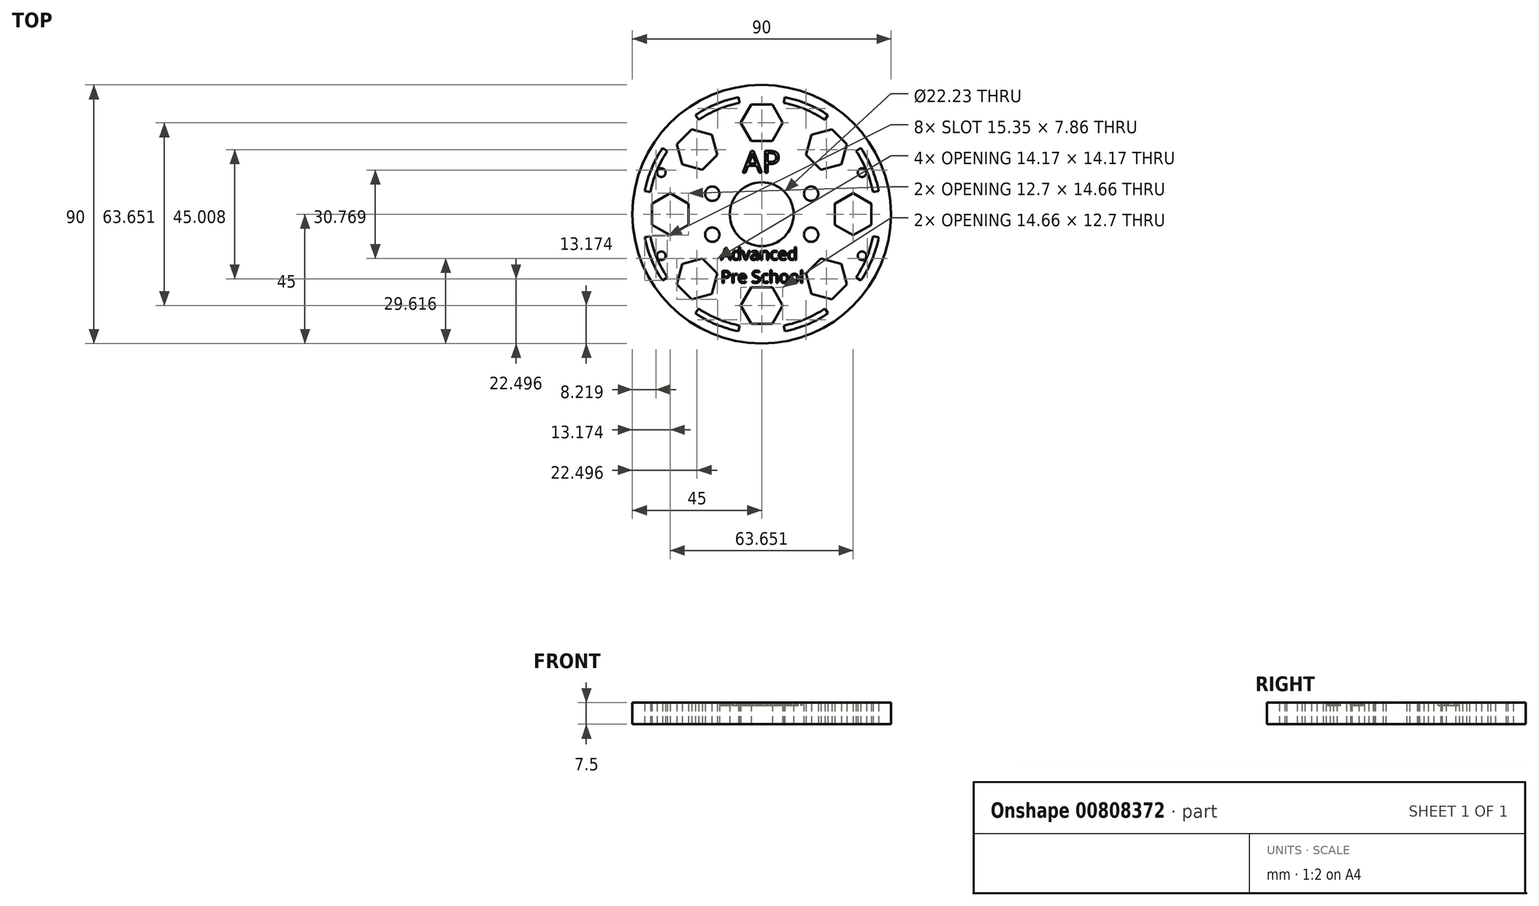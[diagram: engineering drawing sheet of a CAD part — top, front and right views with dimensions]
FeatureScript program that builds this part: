
annotation { "Feature Type Name" : "Feature", "Feature Type Description" : "" }
export const myFeature = defineFeature(function(context is Context, id is Id, definition is map)
    precondition{}
    {
        {
            var Q0;
            Q0=qCreatedBy(makeId("Top.planeOp"),FACE);
            var sketch = newSketch(context, id + "F0", { "sketchPlane" : qUnion([Q0])});
            skCircle(sketch, "E0", {"center": v(0, 0) * mm, "radius": 45 * mm});
            skCircle(sketch, "E1", {"center": v(0, 0) * mm, "radius": 11.11 * mm});
            skCircle(sketch, "E2", {"center": v(0, 31.83) * mm, "radius": 6.35 * mm});
            skCircle(sketch, "E3.cCircle", {"center": v(0, 31.83) * mm, "radius": 6.35 * mm, "construction": true});
            skLineSegment(sketch, "E3.0", {"start": v(-3.67, 38.18) * mm, "end": v(3.67, 38.18) * mm});
            skLineSegment(sketch, "E3.1", {"start": v(3.67, 38.18) * mm, "end": v(7.33, 31.83) * mm});
            skLineSegment(sketch, "E3.2", {"start": v(7.33, 31.83) * mm, "end": v(3.67, 25.48) * mm});
            skLineSegment(sketch, "E3.3", {"start": v(3.67, 25.48) * mm, "end": v(-3.67, 25.48) * mm});
            skLineSegment(sketch, "E3.4", {"start": v(-3.67, 25.48) * mm, "end": v(-7.33, 31.83) * mm});
            skLineSegment(sketch, "E3.5", {"start": v(-7.33, 31.83) * mm, "end": v(-3.67, 38.18) * mm});
            skPoint(sketch, "E3.0.midPoint", {"position": v(0, 38.18) * mm});
            skLineSegment(sketch, "E4.1.0", {"start": v(-15.42, 20.6) * mm, "end": v(-20.6, 15.42) * mm});
            skLineSegment(sketch, "E4.1.1", {"start": v(-17.32, 27.69) * mm, "end": v(-15.42, 20.6) * mm});
            skLineSegment(sketch, "E4.1.2", {"start": v(-20.6, 15.42) * mm, "end": v(-27.69, 17.32) * mm});
            skLineSegment(sketch, "E4.1.3", {"start": v(-27.69, 17.32) * mm, "end": v(-29.59, 24.4) * mm});
            skLineSegment(sketch, "E4.1.4", {"start": v(-29.59, 24.4) * mm, "end": v(-24.4, 29.59) * mm});
            skLineSegment(sketch, "E4.1.5", {"start": v(-24.4, 29.59) * mm, "end": v(-17.32, 27.69) * mm});
            skLineSegment(sketch, "E4.2.0", {"start": v(-25.48, 3.67) * mm, "end": v(-25.48, -3.67) * mm});
            skLineSegment(sketch, "E4.2.1", {"start": v(-31.83, 7.33) * mm, "end": v(-25.48, 3.67) * mm});
            skLineSegment(sketch, "E4.2.2", {"start": v(-25.48, -3.67) * mm, "end": v(-31.83, -7.33) * mm});
            skLineSegment(sketch, "E4.2.3", {"start": v(-31.83, -7.33) * mm, "end": v(-38.18, -3.67) * mm});
            skLineSegment(sketch, "E4.2.4", {"start": v(-38.18, -3.67) * mm, "end": v(-38.18, 3.67) * mm});
            skLineSegment(sketch, "E4.2.5", {"start": v(-38.18, 3.67) * mm, "end": v(-31.83, 7.33) * mm});
            skLineSegment(sketch, "E5.2.3.0", {"start": v(-20.6, -15.42) * mm, "end": v(-15.42, -20.6) * mm});
            skLineSegment(sketch, "E5.3.3.0", {"start": v(-27.69, -17.32) * mm, "end": v(-20.6, -15.42) * mm});
            skLineSegment(sketch, "E5.6.3.0", {"start": v(-15.42, -20.6) * mm, "end": v(-17.32, -27.69) * mm});
            skLineSegment(sketch, "E5.9.3.0", {"start": v(-17.32, -27.69) * mm, "end": v(-24.4, -29.59) * mm});
            skLineSegment(sketch, "E5.12.3.0", {"start": v(-24.4, -29.59) * mm, "end": v(-29.59, -24.4) * mm});
            skLineSegment(sketch, "E5.15.3.0", {"start": v(-29.59, -24.4) * mm, "end": v(-27.69, -17.32) * mm});
            skLineSegment(sketch, "E5.2.4.0", {"start": v(-3.67, -25.48) * mm, "end": v(3.67, -25.48) * mm});
            skLineSegment(sketch, "E5.3.4.0", {"start": v(-7.33, -31.83) * mm, "end": v(-3.67, -25.48) * mm});
            skLineSegment(sketch, "E5.6.4.0", {"start": v(3.67, -25.48) * mm, "end": v(7.33, -31.83) * mm});
            skLineSegment(sketch, "E5.9.4.0", {"start": v(7.33, -31.83) * mm, "end": v(3.67, -38.18) * mm});
            skLineSegment(sketch, "E5.12.4.0", {"start": v(3.67, -38.18) * mm, "end": v(-3.67, -38.18) * mm});
            skLineSegment(sketch, "E5.15.4.0", {"start": v(-3.67, -38.18) * mm, "end": v(-7.33, -31.83) * mm});
            skLineSegment(sketch, "E5.2.5.0", {"start": v(15.42, -20.6) * mm, "end": v(20.6, -15.42) * mm});
            skLineSegment(sketch, "E5.3.5.0", {"start": v(17.32, -27.69) * mm, "end": v(15.42, -20.6) * mm});
            skLineSegment(sketch, "E5.6.5.0", {"start": v(20.6, -15.42) * mm, "end": v(27.69, -17.32) * mm});
            skLineSegment(sketch, "E5.9.5.0", {"start": v(27.69, -17.32) * mm, "end": v(29.59, -24.4) * mm});
            skLineSegment(sketch, "E5.12.5.0", {"start": v(29.59, -24.4) * mm, "end": v(24.4, -29.59) * mm});
            skLineSegment(sketch, "E5.15.5.0", {"start": v(24.4, -29.59) * mm, "end": v(17.32, -27.69) * mm});
            skLineSegment(sketch, "E5.2.6.0", {"start": v(25.48, -3.67) * mm, "end": v(25.48, 3.67) * mm});
            skLineSegment(sketch, "E5.3.6.0", {"start": v(31.83, -7.33) * mm, "end": v(25.48, -3.67) * mm});
            skLineSegment(sketch, "E5.6.6.0", {"start": v(25.48, 3.67) * mm, "end": v(31.83, 7.33) * mm});
            skLineSegment(sketch, "E5.9.6.0", {"start": v(31.83, 7.33) * mm, "end": v(38.18, 3.67) * mm});
            skLineSegment(sketch, "E5.12.6.0", {"start": v(38.18, 3.67) * mm, "end": v(38.18, -3.67) * mm});
            skLineSegment(sketch, "E5.15.6.0", {"start": v(38.18, -3.67) * mm, "end": v(31.83, -7.33) * mm});
            skLineSegment(sketch, "E5.2.7.0", {"start": v(20.6, 15.42) * mm, "end": v(15.42, 20.6) * mm});
            skLineSegment(sketch, "E5.3.7.0", {"start": v(27.69, 17.32) * mm, "end": v(20.6, 15.42) * mm});
            skLineSegment(sketch, "E5.6.7.0", {"start": v(15.42, 20.6) * mm, "end": v(17.32, 27.69) * mm});
            skLineSegment(sketch, "E5.9.7.0", {"start": v(17.32, 27.69) * mm, "end": v(24.4, 29.59) * mm});
            skLineSegment(sketch, "E5.12.7.0", {"start": v(24.4, 29.59) * mm, "end": v(29.59, 24.4) * mm});
            skLineSegment(sketch, "E5.15.7.0", {"start": v(29.59, 24.4) * mm, "end": v(27.69, 17.32) * mm});
            skLineSegment(sketch, "E6.anchor2", {"start": v(0, 0) * mm, "end": v(41.57, -17.22) * mm, "construction": true});
            skCircle(sketch, "E7", {"center": v(17.2, -7.13) * mm, "radius": 2.5 * mm});
            skCircle(sketch, "E8", {"center": v(34.93, -14.47) * mm, "radius": 1.5 * mm});
            skCircle(sketch, "E9.MirrorC", {"center": v(34.93, 14.47) * mm, "radius": 1.5 * mm});
            skCircle(sketch, "E10.MirrorC", {"center": v(17.2, 7.13) * mm, "radius": 2.5 * mm});
            skCircle(sketch, "E11.MirrorC", {"center": v(-17.2, 7.13) * mm, "radius": 2.5 * mm});
            skCircle(sketch, "E12.MirrorC", {"center": v(-34.93, 14.47) * mm, "radius": 1.5 * mm});
            skCircle(sketch, "E13.MirrorC", {"center": v(-17.2, -7.13) * mm, "radius": 2.5 * mm});
            skCircle(sketch, "E14.MirrorC", {"center": v(-34.93, -14.47) * mm, "radius": 1.5 * mm});
            skLineSegment(sketch, "E15", {"start": v(0, 0) * mm, "end": v(0, -45) * mm});
            skLineSegment(sketch, "E16.1.0", {"start": v(0, 0) * mm, "end": v(-2.17, -10.9) * mm});
            skLineSegment(sketch, "E16.3.0", {"start": v(0, 0) * mm, "end": v(-18.76, -28.07) * mm});
            skArc(sketch, "E17", {"start": v(-7.7, -38.75) * mm, "mid": v(-15.12, -36.5) * mm, "end": v(-21.95, -32.85) * mm});
            skArc(sketch, "E18", {"start": v(-8.1, -40.71) * mm, "mid": v(-15.88, -38.35) * mm, "end": v(-23.06, -34.51) * mm});
            skLineSegment(sketch, "E19.trimOffspring", {"start": v(-5.8, -29.18) * mm, "end": v(-6.59, -33.12) * mm});
            skPoint(sketch, "E20.orphan", {"position": v(-25, -37.42) * mm});
            skLineSegment(sketch, "E21.trimOffspring", {"start": v(-21.95, -32.85) * mm, "end": v(-23.06, -34.51) * mm});
            skLineSegment(sketch, "E22.trimOffspring", {"start": v(-7.7, -38.75) * mm, "end": v(-8.1, -40.71) * mm});
            skPoint(sketch, "E23.orphan", {"position": v(-8.78, -44.14) * mm});
            skPoint(sketch, "E24.1.0", {"position": v(8.78, -44.14) * mm});
            skArc(sketch, "E24.1.1", {"start": v(21.95, -32.85) * mm, "mid": v(15.12, -36.5) * mm, "end": v(7.7, -38.75) * mm});
            skArc(sketch, "E24.1.2", {"start": v(23.06, -34.51) * mm, "mid": v(15.88, -38.35) * mm, "end": v(8.1, -40.71) * mm});
            skLineSegment(sketch, "E24.1.3", {"start": v(21.95, -32.85) * mm, "end": v(23.06, -34.51) * mm});
            skLineSegment(sketch, "E24.1.4", {"start": v(7.7, -38.75) * mm, "end": v(8.1, -40.71) * mm});
            skPoint(sketch, "E24.2.0", {"position": v(37.42, -25) * mm});
            skArc(sketch, "E24.2.1", {"start": v(38.75, -7.7) * mm, "mid": v(36.5, -15.12) * mm, "end": v(32.85, -21.95) * mm});
            skArc(sketch, "E24.2.2", {"start": v(40.71, -8.1) * mm, "mid": v(38.35, -15.88) * mm, "end": v(34.51, -23.06) * mm});
            skLineSegment(sketch, "E24.2.3", {"start": v(38.75, -7.7) * mm, "end": v(40.71, -8.1) * mm});
            skLineSegment(sketch, "E24.2.4", {"start": v(32.85, -21.95) * mm, "end": v(34.51, -23.06) * mm});
            skPoint(sketch, "E24.3.0", {"position": v(44.14, 8.78) * mm});
            skArc(sketch, "E24.3.1", {"start": v(32.85, 21.95) * mm, "mid": v(36.5, 15.12) * mm, "end": v(38.75, 7.7) * mm});
            skArc(sketch, "E24.3.2", {"start": v(34.51, 23.06) * mm, "mid": v(38.35, 15.88) * mm, "end": v(40.71, 8.1) * mm});
            skLineSegment(sketch, "E24.3.3", {"start": v(32.85, 21.95) * mm, "end": v(34.51, 23.06) * mm});
            skLineSegment(sketch, "E24.3.4", {"start": v(38.75, 7.7) * mm, "end": v(40.71, 8.1) * mm});
            skPoint(sketch, "E24.4.0", {"position": v(25, 37.42) * mm});
            skArc(sketch, "E24.4.1", {"start": v(7.7, 38.75) * mm, "mid": v(15.12, 36.5) * mm, "end": v(21.95, 32.85) * mm});
            skArc(sketch, "E24.4.2", {"start": v(8.1, 40.71) * mm, "mid": v(15.88, 38.35) * mm, "end": v(23.06, 34.51) * mm});
            skLineSegment(sketch, "E24.4.3", {"start": v(7.7, 38.75) * mm, "end": v(8.1, 40.71) * mm});
            skLineSegment(sketch, "E24.4.4", {"start": v(21.95, 32.85) * mm, "end": v(23.06, 34.51) * mm});
            skPoint(sketch, "E24.5.0", {"position": v(-8.78, 44.14) * mm});
            skArc(sketch, "E24.5.1", {"start": v(-21.95, 32.85) * mm, "mid": v(-15.12, 36.5) * mm, "end": v(-7.7, 38.75) * mm});
            skArc(sketch, "E24.5.2", {"start": v(-23.06, 34.51) * mm, "mid": v(-15.88, 38.35) * mm, "end": v(-8.1, 40.71) * mm});
            skLineSegment(sketch, "E24.5.3", {"start": v(-21.95, 32.85) * mm, "end": v(-23.06, 34.51) * mm});
            skLineSegment(sketch, "E24.5.4", {"start": v(-7.7, 38.75) * mm, "end": v(-8.1, 40.71) * mm});
            skPoint(sketch, "E24.6.0", {"position": v(-37.42, 25) * mm});
            skArc(sketch, "E24.6.1", {"start": v(-38.75, 7.7) * mm, "mid": v(-36.5, 15.12) * mm, "end": v(-32.85, 21.95) * mm});
            skArc(sketch, "E24.6.2", {"start": v(-40.71, 8.1) * mm, "mid": v(-38.35, 15.88) * mm, "end": v(-34.51, 23.06) * mm});
            skLineSegment(sketch, "E24.6.3", {"start": v(-38.75, 7.7) * mm, "end": v(-40.71, 8.1) * mm});
            skLineSegment(sketch, "E24.6.4", {"start": v(-32.85, 21.95) * mm, "end": v(-34.51, 23.06) * mm});
            skPoint(sketch, "E24.7.0", {"position": v(-44.14, -8.78) * mm});
            skArc(sketch, "E24.7.1", {"start": v(-32.85, -21.95) * mm, "mid": v(-36.5, -15.12) * mm, "end": v(-38.75, -7.7) * mm});
            skArc(sketch, "E24.7.2", {"start": v(-34.51, -23.06) * mm, "mid": v(-38.35, -15.88) * mm, "end": v(-40.71, -8.1) * mm});
            skLineSegment(sketch, "E24.7.3", {"start": v(-32.85, -21.95) * mm, "end": v(-34.51, -23.06) * mm});
            skLineSegment(sketch, "E24.7.4", {"start": v(-38.75, -7.7) * mm, "end": v(-40.71, -8.1) * mm});
            skSolve(sketch);
        }
        {
            var Q0;
            {var subQ1=sQuery(id+"F0.wireOp",EDGE,"E5.6.3.0");Q0=makeQuery(id+"F0.imprint","IMPRINT",FACE,{"disambiguationData":[TD([[makeQuery(id+"F0.imprint","IMPRINT",EDGE,{"derivedFrom":subQ1}),1.0]])]});}
            var Q1;
            {var subQ4=sQuery(id+"F0.wireOp",EDGE,"E4.2.2");Q1=makeQuery(id+"F0.imprint","IMPRINT",FACE,{"disambiguationData":[TD([[makeQuery(id+"F0.imprint","IMPRINT",EDGE,{"derivedFrom":subQ4}),1.0]])]});}
            var Q2;
            {var subQ4=sQuery(id+"F0.wireOp",EDGE,"E4.1.2");Q2=makeQuery(id+"F0.imprint","IMPRINT",FACE,{"disambiguationData":[TD([[makeQuery(id+"F0.imprint","IMPRINT",EDGE,{"derivedFrom":subQ4}),1.0]])]});}
            var Q3;
            {var subQ24=sQuery(id+"F0.wireOp",EDGE,"E4.1.1");Q3=makeQuery(id+"F0.imprint","IMPRINT",FACE,{"disambiguationData":[TD([[makeQuery(id+"F0.imprint","IMPRINT",EDGE,{"derivedFrom":subQ24}),1.0]])]});}
            var Q4;
            {var subQ24=sQuery(id+"F0.wireOp",EDGE,"E5.6.7.0");Q4=makeQuery(id+"F0.imprint","IMPRINT",FACE,{"disambiguationData":[TD([[makeQuery(id+"F0.imprint","IMPRINT",EDGE,{"derivedFrom":subQ24}),1.0]])]});}
            var Q5;
            {var subQ4=sQuery(id+"F0.wireOp",EDGE,"E5.6.6.0");Q5=makeQuery(id+"F0.imprint","IMPRINT",FACE,{"disambiguationData":[TD([[makeQuery(id+"F0.imprint","IMPRINT",EDGE,{"derivedFrom":subQ4}),1.0]])]});}
            var Q6;
            {var subQ10=sQuery(id+"F0.wireOp",EDGE,"E5.6.5.0");Q6=makeQuery(id+"F0.imprint","IMPRINT",FACE,{"disambiguationData":[TD([[makeQuery(id+"F0.imprint","IMPRINT",EDGE,{"derivedFrom":subQ10}),1.0]])]});}
            var Q7;
            {var subQ16=sQuery(id+"F0.wireOp",EDGE,"E5.6.4.0");Q7=makeQuery(id+"F0.imprint","IMPRINT",FACE,{"disambiguationData":[TD([[makeQuery(id+"F0.imprint","IMPRINT",EDGE,{"derivedFrom":subQ16}),1.0]])]});}
            extrude(context, id + "F1", {"entities" : qUnion([Q0, Q1, Q2, Q3, Q4, Q5, Q6, Q7]), "depth" : 7.5 * mm, "offsetDistance" : 25 * mm});
        }
        {
            var Q0;
            Q0=makeQuery(id+"F1.opExtrude","CAP_FACE",FACE,{"disambiguationData":[OSD([sQuery(id+"F0.wireOp",EDGE,"E0"),sQuery(id+"F0.wireOp",EDGE,"E1"),sQuery(id+"F0.wireOp",EDGE,"E3.0"),sQuery(id+"F0.wireOp",EDGE,"E3.1"),sQuery(id+"F0.wireOp",EDGE,"E3.2"),sQuery(id+"F0.wireOp",EDGE,"E3.3"),sQuery(id+"F0.wireOp",EDGE,"E3.4"),sQuery(id+"F0.wireOp",EDGE,"E3.5"),sQuery(id+"F0.wireOp",EDGE,"E4.1.0"),sQuery(id+"F0.wireOp",EDGE,"E4.1.1"),sQuery(id+"F0.wireOp",EDGE,"E4.1.2"),sQuery(id+"F0.wireOp",EDGE,"E4.1.3"),sQuery(id+"F0.wireOp",EDGE,"E4.1.4"),sQuery(id+"F0.wireOp",EDGE,"E4.1.5"),sQuery(id+"F0.wireOp",EDGE,"E4.2.0"),sQuery(id+"F0.wireOp",EDGE,"E4.2.1"),sQuery(id+"F0.wireOp",EDGE,"E4.2.2"),sQuery(id+"F0.wireOp",EDGE,"E4.2.3"),sQuery(id+"F0.wireOp",EDGE,"E4.2.4"),sQuery(id+"F0.wireOp",EDGE,"E4.2.5"),sQuery(id+"F0.wireOp",EDGE,"E5.2.3.0"),sQuery(id+"F0.wireOp",EDGE,"E5.3.3.0"),sQuery(id+"F0.wireOp",EDGE,"E5.6.3.0"),sQuery(id+"F0.wireOp",EDGE,"E5.9.3.0"),sQuery(id+"F0.wireOp",EDGE,"E5.12.3.0"),sQuery(id+"F0.wireOp",EDGE,"E5.15.3.0"),sQuery(id+"F0.wireOp",EDGE,"E5.2.4.0"),sQuery(id+"F0.wireOp",EDGE,"E5.3.4.0"),sQuery(id+"F0.wireOp",EDGE,"E5.6.4.0"),sQuery(id+"F0.wireOp",EDGE,"E5.9.4.0"),sQuery(id+"F0.wireOp",EDGE,"E5.12.4.0"),sQuery(id+"F0.wireOp",EDGE,"E5.15.4.0"),sQuery(id+"F0.wireOp",EDGE,"E5.2.5.0"),sQuery(id+"F0.wireOp",EDGE,"E5.3.5.0"),sQuery(id+"F0.wireOp",EDGE,"E5.6.5.0"),sQuery(id+"F0.wireOp",EDGE,"E5.9.5.0"),sQuery(id+"F0.wireOp",EDGE,"E5.12.5.0"),sQuery(id+"F0.wireOp",EDGE,"E5.15.5.0"),sQuery(id+"F0.wireOp",EDGE,"E5.2.6.0"),sQuery(id+"F0.wireOp",EDGE,"E5.3.6.0"),sQuery(id+"F0.wireOp",EDGE,"E5.6.6.0"),sQuery(id+"F0.wireOp",EDGE,"E5.9.6.0"),sQuery(id+"F0.wireOp",EDGE,"E5.12.6.0"),sQuery(id+"F0.wireOp",EDGE,"E5.15.6.0"),sQuery(id+"F0.wireOp",EDGE,"E5.2.7.0"),sQuery(id+"F0.wireOp",EDGE,"E5.3.7.0"),sQuery(id+"F0.wireOp",EDGE,"E5.6.7.0"),sQuery(id+"F0.wireOp",EDGE,"E5.9.7.0"),sQuery(id+"F0.wireOp",EDGE,"E5.12.7.0"),sQuery(id+"F0.wireOp",EDGE,"E5.15.7.0")])],"isStart":false});
            var sketch = newSketch(context, id + "F2", { "sketchPlane" : qUnion([Q0])});
            skText(sketch, "E25", { "text": "AP", "fontName": "OpenSans-Regular.ttf"});
            skText(sketch, "E26", { "text": "Advanced\nPre School", "fontName": "OpenSans-Regular.ttf"});
            const initialGuessF2  = {"E25": [-0.00658, 0.01448, 1, 0, 0.0076], "E26": [-0.01429, -0.01591, 1, 0, 0.00422]};
            skSetInitialGuess(sketch, initialGuessF2);
            skSolve(sketch);
        }
        {
            var Q0;
            Q0 = qSketchRegion(id + "F2", true);
            extrude(context, id + "F3", {"entities" : qUnion([Q0]), "operationType" : NewBodyOperationType.REMOVE, "oppositeDirection" : true, "depth" : 1 * mm, "offsetDistance" : 25 * mm});
        }
    });
